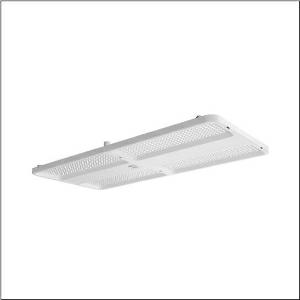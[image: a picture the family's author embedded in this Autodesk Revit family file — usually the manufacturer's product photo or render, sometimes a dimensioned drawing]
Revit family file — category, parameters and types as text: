
# Revit family: highbay_21_maxi_52hn12db4qda03
name_source: partatom
category: Lighting Fixtures
units: mm (PartAtom-declared; Revit-internal decimal feet)

## family parameters
Cut with Voids When Loaded = No
Host = Face
Light Source = No
Part Type = Normal
Room Calculation Point = No
Round Connector Dimension = Use Diameter
Shared = No

## types (1)
- --- (1 x LED, 38000 lm, 197.7 W, 4000K)
    Apparent Load = 198 VA
    CIE Flux Codes = 90 98 100 100 100
    Color Rendering = 80
    Color Temperature = 4000K
    Default Elevation = 1800 mm
    Description = high bay luminaire Highbay 21 maxi; direct symmetric wide distribution, light control with lens of PMMA; UGR ≤ 22 (X = 4H | Y = 8H | S = 0.25H | reflection values 70/50/20); luminous flux: 38.000lm; light colour: 840, colour temperature: 4000K, MacAdam ≤ 3 SDCM (initial), colour rendering: CRI > 80; luminous efficacy: 192,2lm/W; rated service life: 75.000h (L80/B50) at AT= ta max; control: DALI 2; for wired networking: open and standardized DALI2 interface enables full flexibility and future-proofing for changes in use or functional adaptation through individual programming; multi-sensor luminaire consisting of a DALI2 multi-sensor and DALI2 ECG; multi-sensor luminaire for wired connection to a DALI2 application controller (e.g., SITECO Connect 11 or 21); can also be connected to existing on-site lighting or building automation systems upon request; integrated DALI2 sensor certified according to IEC 62386, Parts 101, 103, 303, and 304; integrated DALI2 ECG provides luminaire data (according to IEC 62386, Part 251), energy data (Part 252), and monitoring and analytics data (Part 253) to higher-level systems for further processing; luminaire with PIR sensor (passive-infrared); with light sensor; luminaire connection: terminal, 5-pole, max. 2.5mm² (cable entry for one cable, Ø 8.5..16mm); mains connection: 230..240V, AC 50/60Hz; connected load: 197,7W; protection rating (complete): IP65; insulation class (complete): insulation class I (protective earthing); protection symbol: D; certification: CE, ENEC, VDE, UKCA; internal wiring halogen-free; luminaire corresponds to IFS (International Featured Standards) requirements for safety and quality in the food industry; LABS conformity tested according to VDMA 24364:2018-05; housing frame of high-performance plastic PA6, matt traffic white (RAL 9016); cover of PMMA; dimension (LxWxH): 946 x 442 x 72mm; permissible operating ambient temperature: -20..+40°C (reducing of maximum allowable ambient temperature of 5°C with ceiling mounting); packaging unit: 1 piece; (delivery without accessories; please order mounting accessories separately)
    Height = 72 mm  [stored 0.23622 ft]
    Lamp = 1 x LED
    Lamp Light Flux = 38000 lm
    Lamp Power = 197.7 W
    Lamp count = 1
    Length = 946 mm
    Luminous efficacy = 192 lm/W
    Manufacturer = Siteco
    ModVariant = No
    Model = 52HN12DB4QDA03
    Mounting Place = Ceiling
    Mounting Type = Pendant
    Number of Poles = 1
    OnlyDefault = Yes
    Power Factor = 1
    Product Name = Highbay 21 maxi
    Product group = high bay luminaire
    ProductGroupID = 901
    Protection Class = Protection class I
    Protection Degree = IP 65
    RLX_Detail_Level = 1
    RLX_Emergency_Light_Flux = 0 lm
    RLX_Emergency_Type = 0
    RLX_Emergency_Type_DB = No
    RlxData = <blob elided: 127801 chars, md5=c9ee6a9b>
    Socket = socket
    Standby Power = 0 W
    System Light Flux = 38000 lm
    System Power = 198 W
    Type Comments = factory setting: luminous flux: 100 % | dim-lin: 254 | 918 mA
    Type Image = l_1363267.jpg
    URL = http://relux.com
    VarID = @adj_011535
    Voltage = 0 V
    Weight = 0.00 kg
    Width = 442 mm

note: [stored X ft] marks values corroborated as IEEE doubles in the binary element streams (Revit-internal decimal feet)

## geometry (parser evidence)
native form markers: Blend x4, Sweep x11
no freeform markers — native parametric forms only
